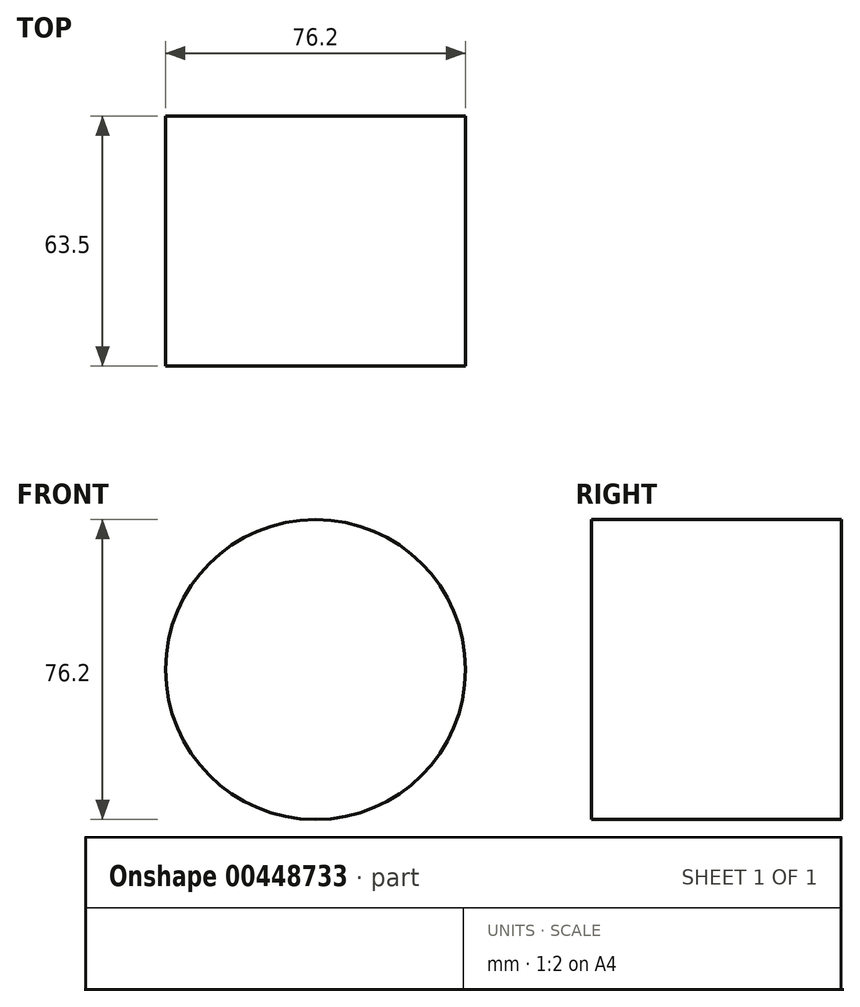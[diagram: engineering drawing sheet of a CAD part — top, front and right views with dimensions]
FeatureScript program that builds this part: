
annotation { "Feature Type Name" : "Feature", "Feature Type Description" : "" }
export const myFeature = defineFeature(function(context is Context, id is Id, definition is map)
    precondition{}
    {
        {
            var Q0;
            Q0=qCreatedBy(makeId("Front.planeOp"),FACE);
            var sketch = newSketch(context, id + "F0", { "sketchPlane" : qUnion([Q0])});
            skCircle(sketch, "E0", {"center": v(0, 0) * mm, "radius": 38.1 * mm});
            skSolve(sketch);
        }
        {
            var Q0;
            Q0 = qSketchRegion(id + "F0", true);
            var Q1;
            Q1=sQuery(id+"F0.wireOp",EDGE,"E0");
            extrude(context, id + "F1", {"entities" : qUnion([Q0]), "surfaceEntities" : qUnion([Q1]), "depth" : 63.5 * mm});
        }
    });
